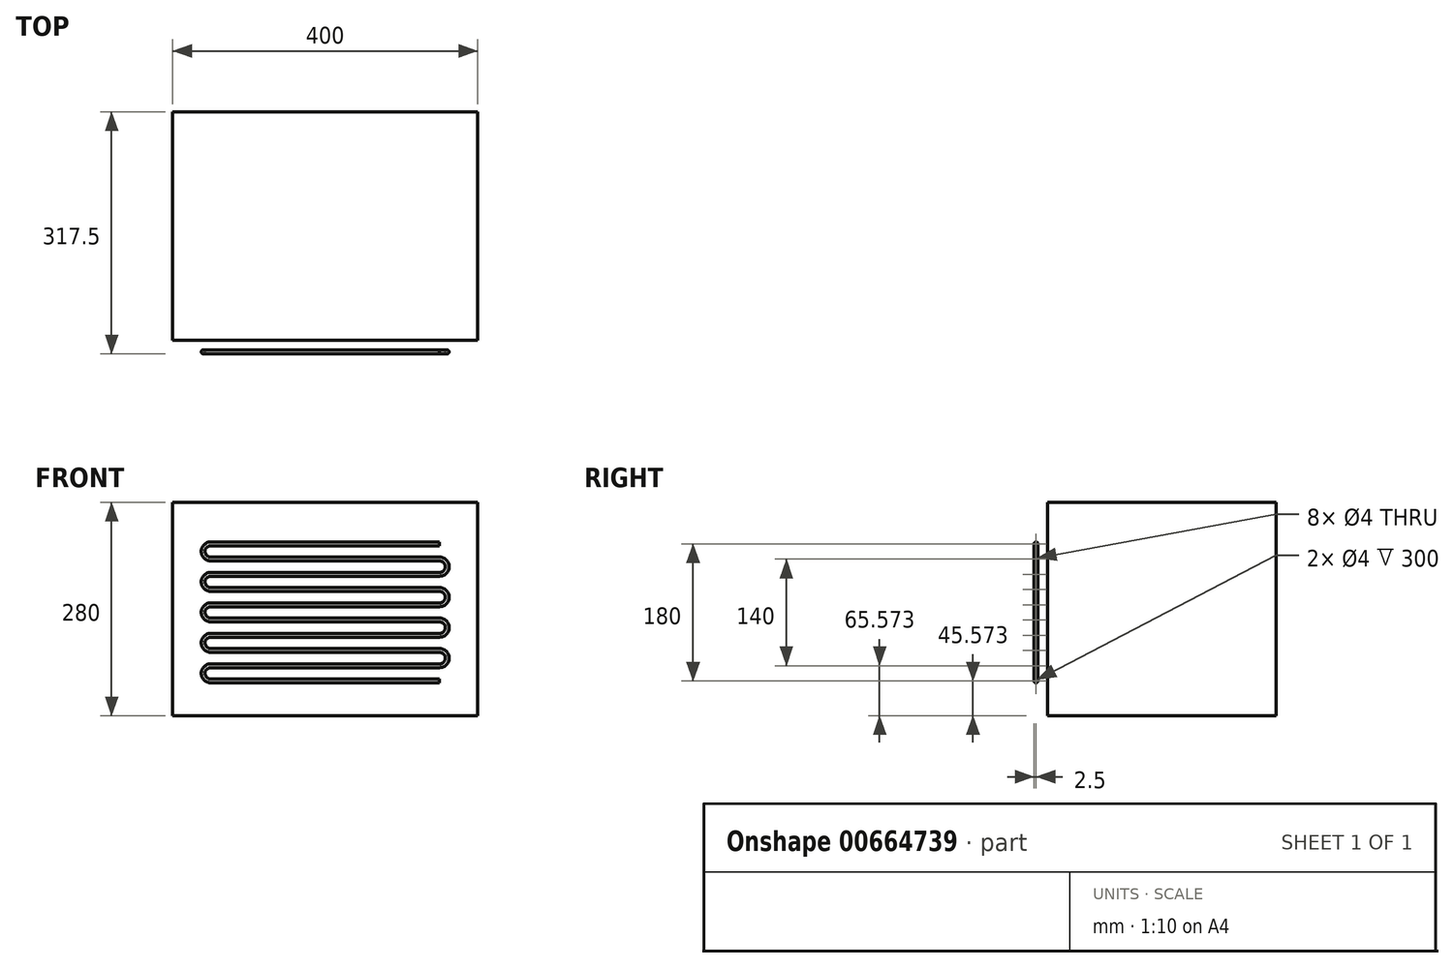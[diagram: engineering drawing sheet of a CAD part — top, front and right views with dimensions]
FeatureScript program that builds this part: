
annotation { "Feature Type Name" : "Feature", "Feature Type Description" : "" }
export const myFeature = defineFeature(function(context is Context, id is Id, definition is map)
    precondition{}
    {
        {
            var Q0;
            Q0=qCreatedBy(makeId("Front.planeOp"),FACE);
            var sketch = newSketch(context, id + "F0", { "sketchPlane" : qUnion([Q0])});
            skLineSegment(sketch, "E0", {"start": v(-150, 25.57) * mm, "end": v(150, 25.57) * mm});
            skLineSegment(sketch, "E1.0.1.0", {"start": v(-150, 5.57) * mm, "end": v(150, 5.57) * mm});
            skLineSegment(sketch, "E1.0.2.0", {"start": v(-150, -14.43) * mm, "end": v(150, -14.43) * mm});
            skLineSegment(sketch, "E1.0.3.0", {"start": v(-150, -34.43) * mm, "end": v(150, -34.43) * mm});
            skLineSegment(sketch, "E1.0.4.0", {"start": v(-150, -54.43) * mm, "end": v(150, -54.43) * mm});
            skLineSegment(sketch, "E1.0.5.0", {"start": v(-150, -74.43) * mm, "end": v(150, -74.43) * mm});
            skLineSegment(sketch, "E1.0.6.0", {"start": v(-150, -94.43) * mm, "end": v(150, -94.43) * mm});
            skLineSegment(sketch, "E1.0.7.0", {"start": v(-150, -114.43) * mm, "end": v(150, -114.43) * mm});
            skLineSegment(sketch, "E1.0.8.0", {"start": v(-150, -134.43) * mm, "end": v(150, -134.43) * mm});
            skLineSegment(sketch, "E1.0.9.0", {"start": v(-150, -154.43) * mm, "end": v(150, -154.43) * mm});
            skLineSegment(sketch, "E1.direction1", {"start": v(-150, 25.57) * mm, "end": v(-150, 25.57) * mm});
            skLineSegment(sketch, "E1.direction2", {"start": v(-150, 25.57) * mm, "end": v(-150, 5.57) * mm, "construction": true});
            skArc(sketch, "E2", {"start": v(-150, 25.57) * mm, "mid": v(-160, 15.57) * mm, "end": v(-150, 5.57) * mm});
            skArc(sketch, "E3", {"start": v(150, 5.57) * mm, "mid": v(160, -4.43) * mm, "end": v(150, -14.43) * mm});
            skArc(sketch, "E4.0.1.0", {"start": v(150, -34.43) * mm, "mid": v(160, -44.43) * mm, "end": v(150, -54.43) * mm});
            skArc(sketch, "E4.0.2.0", {"start": v(150, -74.43) * mm, "mid": v(160, -84.43) * mm, "end": v(150, -94.43) * mm});
            skArc(sketch, "E4.0.3.0", {"start": v(150, -114.43) * mm, "mid": v(160, -124.43) * mm, "end": v(150, -134.43) * mm});
            skLineSegment(sketch, "E4.direction1", {"start": v(150, -14.43) * mm, "end": v(175, -14.43) * mm, "construction": true});
            skLineSegment(sketch, "E4.direction2", {"start": v(150, -14.43) * mm, "end": v(150, -54.43) * mm, "construction": true});
            skArc(sketch, "E5.0.1.0", {"start": v(-150, -14.43) * mm, "mid": v(-160, -24.43) * mm, "end": v(-150, -34.43) * mm});
            skArc(sketch, "E5.0.2.0", {"start": v(-150, -54.43) * mm, "mid": v(-160, -64.43) * mm, "end": v(-150, -74.43) * mm});
            skArc(sketch, "E5.0.3.0", {"start": v(-150, -94.43) * mm, "mid": v(-160, -104.43) * mm, "end": v(-150, -114.43) * mm});
            skArc(sketch, "E5.0.4.0", {"start": v(-150, -134.43) * mm, "mid": v(-160, -144.43) * mm, "end": v(-150, -154.43) * mm});
            skLineSegment(sketch, "E5.direction1", {"start": v(-150, 5.57) * mm, "end": v(-125, 5.57) * mm, "construction": true});
            skLineSegment(sketch, "E5.direction2", {"start": v(-150, 5.57) * mm, "end": v(-150, -34.43) * mm, "construction": true});
            skSolve(sketch);
        }
        {
            var Q0;
            Q0=qCreatedBy(makeId("Right.planeOp"),FACE);
            var sketch = newSketch(context, id + "F1", { "sketchPlane" : qUnion([Q0])});
            skCircle(sketch, "E6", {"center": v(0, 25.57) * mm, "radius": 2.5 * mm});
            skCircle(sketch, "E7", {"center": v(0, 25.57) * mm, "radius": 2 * mm});
            skSolve(sketch);
        }
        {
            var Q0;
            Q0 = qSketchRegion(id + "F1", true);
            var Q1;
            Q1 = qConstructionFilter(qBodyType(qCreatedBy(id + "F0" ,EDGE), BodyType.WIRE), ConstructionObject.NO);
            sweep(context, id + "F2", {"profiles" : qUnion([Q0]), "path" : qUnion([Q1])});
        }
        {
            var Q0;
            Q0=qCreatedBy(makeId("Top.planeOp"),FACE);
            var sketch = newSketch(context, id + "F3", { "sketchPlane" : qUnion([Q0])});
            skLineSegment(sketch, "E8.bottom", {"start": v(-200, 15) * mm, "end": v(200, 15) * mm});
            skLineSegment(sketch, "E8.top", {"start": v(-200, 315) * mm, "end": v(200, 315) * mm});
            skLineSegment(sketch, "E8.left", {"start": v(-200, 15) * mm, "end": v(-200, 315) * mm});
            skLineSegment(sketch, "E8.right", {"start": v(200, 15) * mm, "end": v(200, 315) * mm});
            skSolve(sketch);
        }
        {
            var Q0;
            Q0 = qSketchRegion(id + "F3", true);
            extrude(context, id + "F4", {"entities" : qUnion([Q0]), "depth" : 80 * mm, "offsetDistance" : 25 * mm, "hasSecondDirection" : true, "secondDirectionOppositeDirection" : true, "secondDirectionDepth" : 200 * mm});
        }
    });
